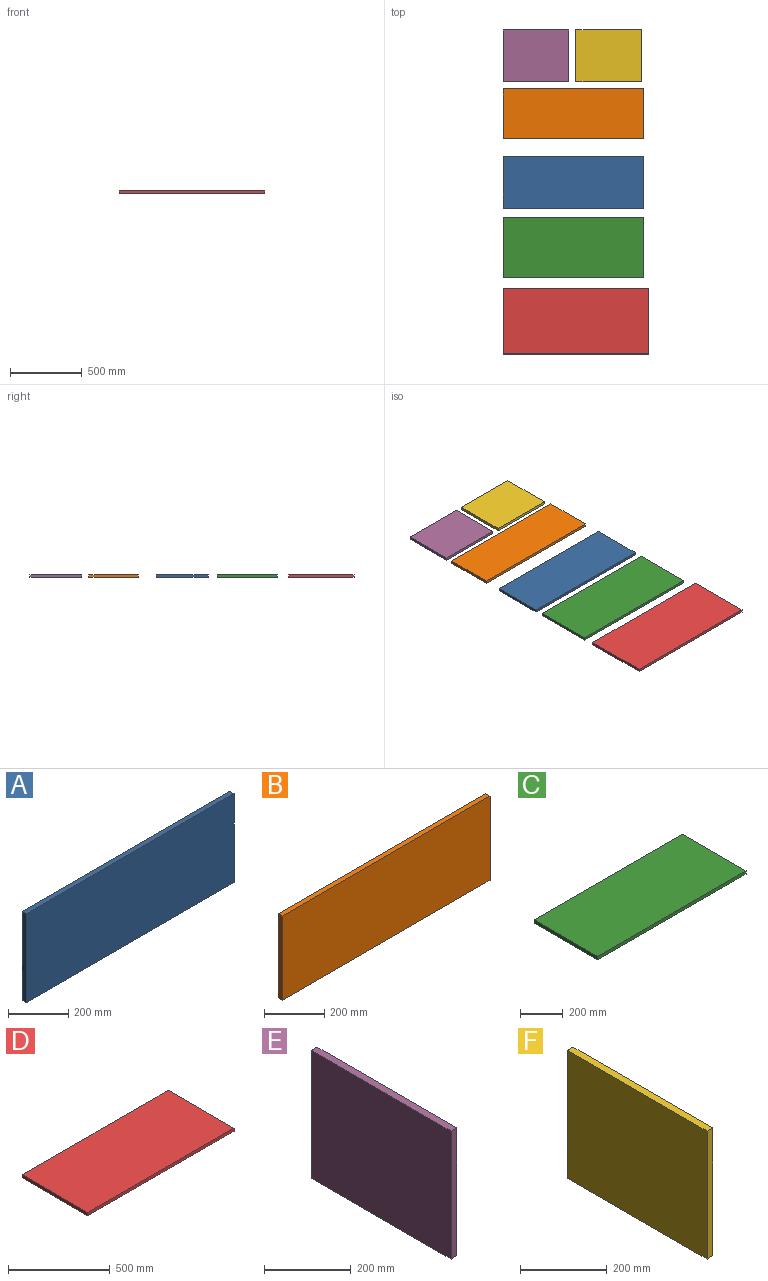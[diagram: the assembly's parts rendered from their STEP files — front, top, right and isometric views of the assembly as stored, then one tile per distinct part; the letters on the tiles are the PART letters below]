
ASSEMBLY  parts=6 mates=10
PART A: 6 faces, bbox 977.9x19.1x362 mm
  f0: plane 361.95x19.05mm, normal (1,0,0), area 6895.1mm2, adj f1,f3,f4,f5
  f1: plane 977.9x19.05mm, normal (0,0,-1), area 18629mm2, adj f0,f2,f4,f5
  f2: plane 361.95x19.05mm, normal (-1,0,0), area 6895.1mm2, adj f1,f3,f4,f5
  f3: plane 977.9x19.05mm, normal (0,0,1), area 18629mm2, adj f0,f2,f4,f5
  f4: plane 977.9x361.95mm, normal (0,1,0), area 353950.9mm2, adj f0,f1,f2,f3
  f5: plane 977.9x361.95mm, normal (0,-1,0), area 353950.9mm2, adj f0,f1,f2,f3
PART B: 6 faces, bbox 977.9x19.1x342.9 mm
  f0: plane 342.9x19.05mm, normal (-1,0,0), area 6532.2mm2, adj f1,f3,f4,f5
  f1: plane 977.9x19.05mm, normal (0,0,-1), area 18629mm2, adj f0,f2,f4,f5
  f2: plane 342.9x19.05mm, normal (1,0,0), area 6532.2mm2, adj f1,f3,f4,f5
  f3: plane 977.9x19.05mm, normal (0,0,1), area 18629mm2, adj f0,f2,f4,f5
  f4: plane 977.9x342.9mm, normal (0,-1,0), area 335321.9mm2, adj f0,f1,f2,f3
  f5: plane 977.9x342.9mm, normal (0,1,0), area 335321.9mm2, adj f0,f1,f2,f3
PART C: 6 faces, bbox 977.9x419.1x19.1 mm
  f0: plane 419.1x19.05mm, normal (1,0,0), area 7983.9mm2, adj f1,f3,f4,f5
  f1: plane 977.9x19.05mm, normal (0,1,0), area 18629mm2, adj f0,f2,f4,f5
  f2: plane 419.1x19.05mm, normal (-1,0,0), area 7983.9mm2, adj f1,f3,f4,f5
  f3: plane 977.9x19.05mm, normal (0,-1,0), area 18629mm2, adj f0,f2,f4,f5
  f4: plane 977.9x419.1mm, normal (0,0,1), area 409837.9mm2, adj f0,f1,f2,f3
  f5: plane 977.9x419.1mm, normal (0,0,-1), area 409837.9mm2, adj f0,f1,f2,f3
PART D: 6 faces, bbox 1016x457.2x19.1 mm
  f0: plane 1016x19.05mm, normal (0,1,0), area 19354.8mm2, adj f1,f3,f4,f5
  f1: plane 457.2x19.05mm, normal (-1,0,0), area 8709.7mm2, adj f0,f2,f4,f5
  f2: plane 1016x19.05mm, normal (0,-1,0), area 19354.8mm2, adj f1,f3,f4,f5
  f3: plane 457.2x19.05mm, normal (1,0,0), area 8709.7mm2, adj f0,f2,f4,f5
  f4: plane 1016x457.2mm, normal (0,0,1), area 464515.2mm2, adj f0,f1,f2,f3
  f5: plane 1016x457.2mm, normal (0,0,-1), area 464515.2mm2, adj f0,f1,f2,f3
PART E: 6 faces, bbox 19.1x457.2x362 mm
  f0: plane 361.95x19.05mm, normal (0,-1,0), area 6895.1mm2, adj f1,f3,f4,f5
  f1: plane 457.2x19.05mm, normal (0,0,-1), area 8709.7mm2, adj f0,f2,f4,f5
  f2: plane 361.95x19.05mm, normal (0,1,0), area 6895.1mm2, adj f1,f3,f4,f5
  f3: plane 457.2x19.05mm, normal (0,0,1), area 8709.7mm2, adj f0,f2,f4,f5
  f4: plane 457.2x361.95mm, normal (1,0,0), area 165483.5mm2, adj f0,f1,f2,f3
  f5: plane 457.2x361.95mm, normal (-1,0,0), area 165483.5mm2, adj f0,f1,f2,f3
PART F: 6 faces, bbox 19.1x457.2x362 mm
  f0: plane 361.95x19.05mm, normal (0,-1,0), area 6895.1mm2, adj f1,f3,f4,f5
  f1: plane 457.2x19.05mm, normal (0,0,-1), area 8709.7mm2, adj f0,f2,f4,f5
  f2: plane 361.95x19.05mm, normal (0,1,0), area 6895.1mm2, adj f1,f3,f4,f5
  f3: plane 457.2x19.05mm, normal (0,0,1), area 8709.7mm2, adj f0,f2,f4,f5
  f4: plane 457.2x361.95mm, normal (1,0,0), area 165483.5mm2, adj f0,f1,f2,f3
  f5: plane 457.2x361.95mm, normal (-1,0,0), area 165483.5mm2, adj f0,f1,f2,f3
PLACE A rot(axis=(-1,0,0),90deg) t=(0,290.61,228.6)mm
PLACE B rot(axis=(-1,0,0),90deg) t=(0,761.19,-209.55)mm
PLACE C at identity fixed
PLACE D t=(19.05,-517.59,-342.9)mm
PLACE E rot(axis=(0.58,0.58,-0.58),120deg) t=(-260.35,1496.91,-488.95)mm
PLACE F rot(axis=(-0.58,-0.58,-0.58),120deg) t=(247.3,1173.06,-488.95)mm
MATE planar E.f0 <-> B.f0  axis (-1,0,0) through (-488.95,1334.99,9.53)mm
MATE planar D.f4 <-> C.f4  axis (0,0,1) through (19.05,-517.59,19.05)mm
MATE planar A.f5 <-> C.f4  axis (0,0,1) through (0,452.53,19.05)mm
MATE planar F.f4 <-> C.f4  axis (0,0,1) through (247.3,1334.99,19.05)mm
MATE planar C.f2 <-> D.f1  axis (-1,0,0) through (-488.95,0,9.52)mm
MATE planar A.f2 <-> C.f2  axis (-1,0,0) through (-488.95,452.53,9.53)mm
MATE planar B.f0 <-> A.f2  axis (-1,0,0) through (-488.95,932.64,9.53)mm
MATE planar F.f3 <-> E.f1  axis (0,1,0) through (247.3,1515.96,9.52)mm
MATE planar B.f4 <-> C.f4  axis (0,0,1) through (0,932.64,19.05)mm
MATE planar E.f5 <-> C.f4  axis (0,0,1) through (-260.35,1334.99,19.05)mm
